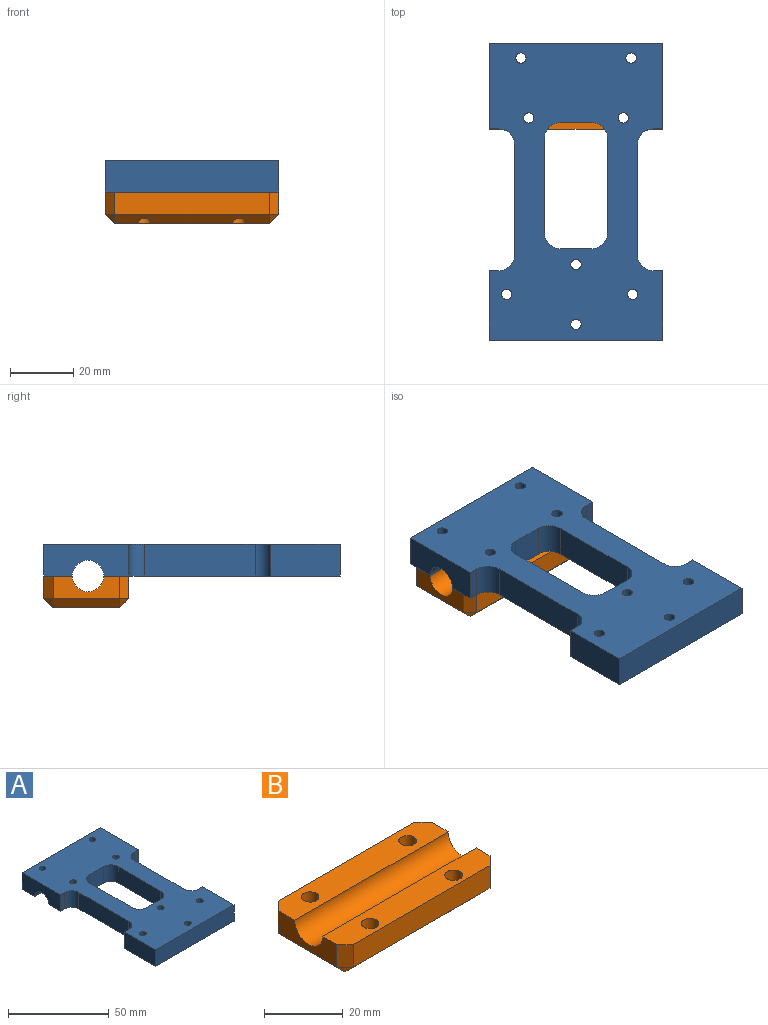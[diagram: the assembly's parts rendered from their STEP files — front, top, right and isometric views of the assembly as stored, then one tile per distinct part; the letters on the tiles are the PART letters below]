
ASSEMBLY  parts=2 mates=1
PART A: 40 faces, bbox 55x94x10 mm
  f0: plane 22x10mm, normal (-1,0,0), area 220mm2, adj f2,f3,f8,f31
  f1: plane 22x10mm, normal (1,0,0), area 220mm2, adj f2,f3,f8,f39
  f2: plane 94x55mm, normal (0,0,1), area 3624.5mm2, adj f0,f1,f4,f6,f7,f8,f9,f11
  f3: plane 75x55mm, normal (0,0,-1), area 2517.7mm2, adj f0,f1,f4,f6,f8,f10,f12,f14
  f4: plane 27x10mm, normal (-1,0,0), area 230.7mm2, adj f2,f3,f5,f7,f17,f30
  f5: plane 55x9mm, normal (0,0,-1), area 477.9mm2, adj f4,f6,f7,f17,f20,f21
  f6: plane 27x10mm, normal (1,0,0), area 230.7mm2, adj f2,f3,f5,f7,f17,f35
  f7: plane 55x10mm, normal (0,1,0), area 550mm2, adj f2,f4,f5,f6
  f8: plane 55x10mm, normal (0,-1,0), area 550mm2, adj f0,f1,f2,f3
  f9: cylinder r=1.65mm len=8.65mm, axis (0,0,-1), area 89.7mm2, adj f2,f10
  f10: cone r=1.65mm half-angle=45deg, axis (0,0,-1), area 27.9mm2, adj f3,f9
  f11: cylinder r=1.65mm len=8.65mm, axis (0,0,-1), area 89.7mm2, adj f2,f12
  f12: cone r=1.65mm half-angle=45deg, axis (0,0,-1), area 27.9mm2, adj f3,f11
  f13: cylinder r=1.65mm len=8.65mm, axis (0,0,-1), area 89.7mm2, adj f2,f14
  f14: cone r=1.65mm half-angle=45deg, axis (0,0,-1), area 27.9mm2, adj f3,f13
  f15: cylinder r=1.65mm len=8.65mm, axis (0,0,-1), area 89.7mm2, adj f2,f16
  f16: cone r=1.65mm half-angle=45deg, axis (0,0,-1), area 27.9mm2, adj f3,f15
  f17: cylinder r=5mm len=55mm, axis (-1,0,0), area 863.9mm2, adj f3,f4,f5,f6
  f18: cylinder r=1.65mm len=10mm, axis (0,0,-1), area 103.7mm2, adj f2,f3
  f19: cylinder r=1.65mm len=10mm, axis (0,0,-1), area 103.7mm2, adj f2,f3
  f20: cylinder r=1.65mm len=10mm, axis (0,0,-1), area 103.7mm2, adj f2,f5
  f21: cylinder r=1.65mm len=10mm, axis (0,0,-1), area 103.7mm2, adj f2,f5
  f22: plane 30x10mm, normal (-1,0,0), area 300mm2, adj f2,f3,f23,f29
  f23: cylinder r=5mm len=10mm, axis (0,0,1), area 78.5mm2, adj f2,f3,f22,f24
  f24: plane 10x10mm, normal (0,-1,0), area 100mm2, adj f2,f3,f23,f25
  f25: cylinder r=5mm len=10mm, axis (0,0,1), area 78.5mm2, adj f2,f3,f24,f26
  f26: plane 30x10mm, normal (1,0,0), area 300mm2, adj f2,f3,f25,f27
  f27: cylinder r=5mm len=10mm, axis (0,0,1), area 78.5mm2, adj f2,f3,f26,f28
  f28: plane 10x10mm, normal (0,1,0), area 100mm2, adj f2,f3,f27,f29
  f29: cylinder r=5mm len=10mm, axis (0,0,1), area 78.5mm2, adj f2,f3,f22,f28
  f30: plane 10x3mm, normal (0,-1,0), area 30mm2, adj f2,f3,f4,f34
  f31: plane 10x3mm, normal (0,1,0), area 30mm2, adj f0,f2,f3,f32
  f32: cylinder r=5mm len=10mm, axis (0,0,1), area 78.5mm2, adj f2,f3,f31,f33
  f33: plane 35x10mm, normal (-1,0,0), area 350mm2, adj f2,f3,f32,f34
  f34: cylinder r=5mm len=10mm, axis (0,0,1), area 78.5mm2, adj f2,f3,f30,f33
  f35: plane 10x3mm, normal (0,-1,0), area 30mm2, adj f2,f3,f6,f36
  f36: cylinder r=5mm len=10mm, axis (0,0,1), area 78.5mm2, adj f2,f3,f35,f37
  f37: plane 35x10mm, normal (1,0,0), area 350mm2, adj f2,f3,f36,f38
  f38: cylinder r=5mm len=10mm, axis (0,0,1), area 78.5mm2, adj f2,f3,f37,f39
  f39: plane 10x3mm, normal (0,1,0), area 30mm2, adj f1,f2,f3,f38
PART B: 24 faces, bbox 55x27x10 mm
  f0: plane 55x9mm, normal (0,0,1), area 454.2mm2, adj f1,f3,f4,f7,f8,f13,f22,f23
  f1: plane 21x7mm, normal (1,0,0), area 107.7mm2, adj f0,f5,f7,f8,f10,f11
  f2: plane 49x7mm, normal (0,-1,0), area 343mm2, adj f5,f10,f16,f19
  f3: plane 49x7mm, normal (0,1,0), area 343mm2, adj f0,f8,f12,f13
  f4: plane 21x7mm, normal (-1,0,0), area 107.7mm2, adj f0,f5,f7,f13,f17,f19
  f5: plane 55x8mm, normal (0,0,1), area 399.2mm2, adj f1,f2,f4,f7,f10,f19,f20,f21
  f6: plane 49x21mm, normal (0,0,-1), area 980.3mm2, adj f11,f12,f16,f17,f20,f21,f22,f23
  f7: cylinder r=5mm len=55mm, axis (1,0,0), area 863.9mm2, adj f0,f1,f4,f5
  f8: plane 7x3mm, normal (0.71,0.71,0), area 29.7mm2, adj f0,f1,f3,f9
  f9: plane 3x3mm, normal (0.58,0.58,-0.58), area 7.8mm2, adj f8,f11,f12
  f10: plane 7x3mm, normal (0.71,-0.71,0), area 29.7mm2, adj f1,f2,f5,f14
  f11: plane 21x3mm, normal (0.71,0,-0.71), area 89.1mm2, adj f1,f6,f9,f14
  f12: plane 49x3mm, normal (0,0.71,-0.71), area 203mm2, adj f3,f6,f9,f15,f22,f23
  f13: plane 7x3mm, normal (-0.71,0.71,0), area 29.7mm2, adj f0,f3,f4,f15
  f14: plane 3x3mm, normal (0.58,-0.58,-0.58), area 7.8mm2, adj f10,f11,f16
  f15: plane 3x3mm, normal (-0.58,0.58,-0.58), area 7.8mm2, adj f12,f13,f17
  f16: plane 49x3mm, normal (0,-0.71,-0.71), area 191.7mm2, adj f2,f6,f14,f18,f20,f21
  f17: plane 21x3mm, normal (-0.71,0,-0.71), area 89.1mm2, adj f4,f6,f15,f18
  f18: plane 3x3mm, normal (-0.58,-0.58,-0.58), area 7.8mm2, adj f16,f17,f19
  f19: plane 7x3mm, normal (-0.71,-0.71,0), area 29.7mm2, adj f2,f4,f5,f18
  f20: cylinder r=2.25mm len=10mm, axis (0,0,1), area 134.5mm2, adj f5,f6,f16
  f21: cylinder r=2.25mm len=10mm, axis (0,0,1), area 134.5mm2, adj f5,f6,f16
  f22: cylinder r=2.25mm len=10mm, axis (0,0,1), area 139.5mm2, adj f0,f6,f12
  f23: cylinder r=2.25mm len=10mm, axis (0,0,1), area 139.5mm2, adj f0,f6,f12
PLACE A t=(-0.08,-0.07,-4.87)mm
PLACE B t=(-0.08,33.43,-14.87)mm
MATE fastened B.f7 <-> A.f17  axis (1,0,0) through (27.42,32.93,-4.87)mm
